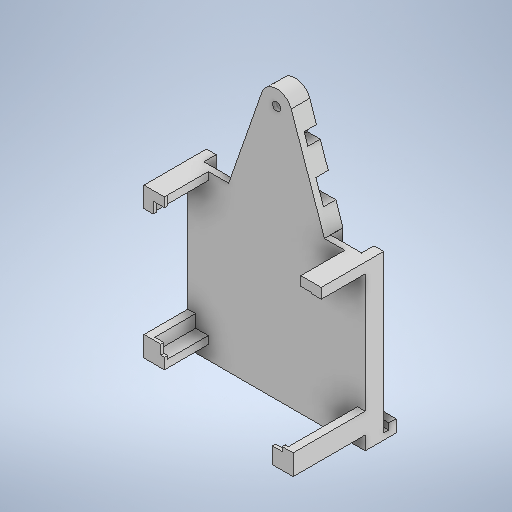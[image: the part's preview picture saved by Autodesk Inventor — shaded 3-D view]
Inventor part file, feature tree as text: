
AUTODESK INVENTOR PART (.ipt)
format: ipt  version: 2025 (Build 290162010, 162A)  size: 925,696 bytes
history: native  units: in
note: dims shown in document units (in); Inventor stores cm internally (conversion verified against a paired STEP export)
features: sketch x9, extrude x8, hole x1
ambient origin geometry x8: Origin, YZ Plane, XZ Plane, XY Plane, X Axis, Y Axis, Z Axis, Center Point
bodies: Solid1 (feature_tree)
feature tree (18):
  extrude  "Extrusion1"  Depth=0.3937in
  extrude  "Extrusion2"  Depth=0.1378in
  extrude  "Extrusion3"  Depth=0.6063in
  extrude  "Extrusion4"  Depth=0.4429in
  extrude  "Extrusion5"  Depth=0.6098in
  extrude  "Extrusion6"  Depth=0.75in
  extrude  "Extrusion8"  Depth=0.1575in
  hole  "Hole1"  [1 undecoded]
  extrude  "Extrusion13"  Depth=0.3937in
  sketch  "Sketch1"  dims[d2=0.3937in d3=1.1516in]
  sketch  "Sketch2"  dims[d4=0.0787in d5=0.0in d6=0.1378in d9=0.1378in d16=0.1378in]
  sketch  "Sketch3"  dims[d22=1.0039in d23=0.6063in]
  sketch  "Sketch4"  dims[d24=0.4429in d25=0.4429in]
  sketch  "Sketch5"  dims[d26=1.2197in d27=0.6098in]
  sketch  "Sketch6"  dims[d28=0.0in d38=0.75in]
  sketch  "Sketch9"  dims[d40=0.1575in d41=0.0in d44=0.1561in]
  sketch  "Sketch11"  dims[d45=0.2061in d46=0.0128in]
  sketch  "Sketch15"  dims[d47=0.1352in d48=0.83in d49=0.35in d50=0.25in d51=0.0787in d58=0.2598in d59=0.2598in d60=0.2598in d61=0.1299in d63=0.0984in d69=0.0984in d70=0.0984in d73=0.52in d74=0.0in d75=0.2618in d76=0.2618in d77=0.0984in d78=0.0984in d79=0.878in d80=0.0in d81=0.26in d82=0.26in d83=0.0197in d84=0.0197in d87=0.0197in d88=0.0197in d89=0.0394in d90=0.0in d93=0.2075in d94=0.1378in d95=0.0394in d96=0.0in d97=1.7094in d100=0.2598in d101=0.2598in d102=0.0984in d103=0.0984in d104=1.7094in d105=0.1378in d106=0.2126in d112=2.2559in d113=1.128in d114=3.2323in d115=0.0984in d116=0.0654in d118=0.1575in d119=0.0787in d120=0.52in d121=0.0in d130=0.104in d131=0.17in d132=0.375in d133=0.25in d134=0.5635in d135=0.4322in d136=0.0in d138=0.2756in d139=0.2756in d140=0.1378in d141=0.1378in d142=0.1378in d143=0.175in d144=0.05in d151=0.3937in d152=0.0in]
note: 1 required parameter value undecoded (feature->parameter linkage not recoverable at this tier; creation-order binding heuristic only, values carry confidence <= 0.55)
